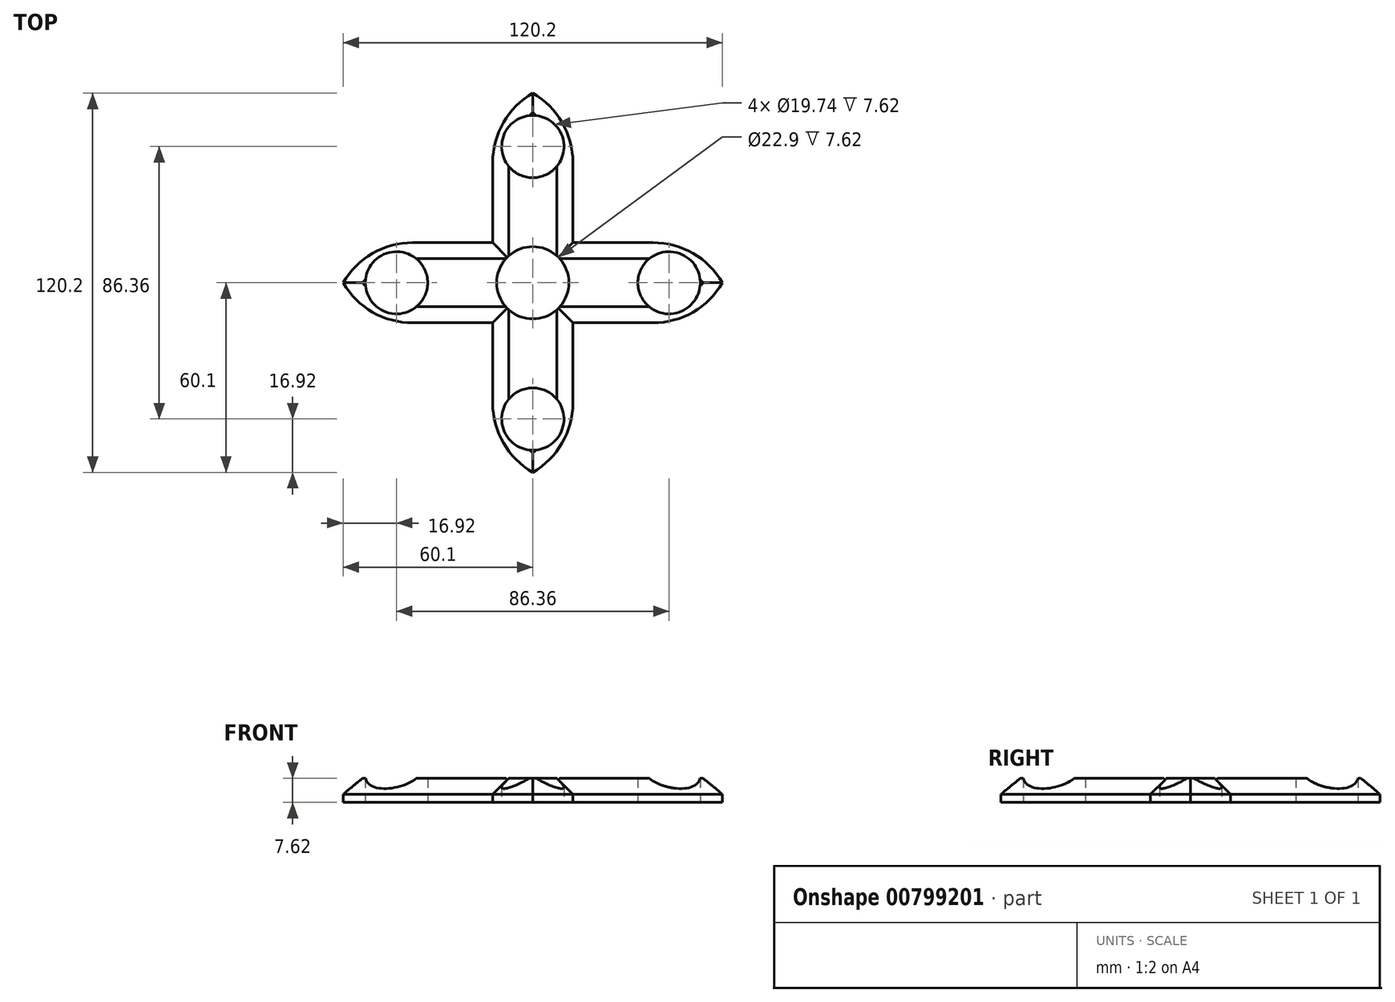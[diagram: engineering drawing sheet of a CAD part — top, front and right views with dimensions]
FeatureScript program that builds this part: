
annotation { "Feature Type Name" : "Feature", "Feature Type Description" : "" }
export const myFeature = defineFeature(function(context is Context, id is Id, definition is map)
    precondition{}
    {
        {
            var Q0;
            Q0=qCreatedBy(makeId("Top.planeOp"),FACE);
            var sketch = newSketch(context, id + "F0", { "sketchPlane" : qUnion([Q0])});
            skLineSegment(sketch, "E0.bottom", {"start": v(12.7, -38.1) * mm, "end": v(-12.7, -38.1) * mm});
            skLineSegment(sketch, "E0.top", {"start": v(12.7, 38.1) * mm, "end": v(-12.7, 38.1) * mm});
            skLineSegment(sketch, "E0.left", {"start": v(12.7, -38.1) * mm, "end": v(12.7, 38.1) * mm});
            skLineSegment(sketch, "E0.right", {"start": v(-12.7, -38.1) * mm, "end": v(-12.7, 38.1) * mm});
            skPoint(sketch, "E0.middle", {"position": v(0, 0) * mm});
            skLineSegment(sketch, "E1.bottom", {"start": v(38.1, -12.7) * mm, "end": v(-38.1, -12.7) * mm});
            skLineSegment(sketch, "E1.top", {"start": v(38.1, 12.7) * mm, "end": v(-38.1, 12.7) * mm});
            skLineSegment(sketch, "E1.left", {"start": v(38.1, -12.7) * mm, "end": v(38.1, 12.7) * mm});
            skLineSegment(sketch, "E1.right", {"start": v(-38.1, -12.7) * mm, "end": v(-38.1, 12.7) * mm});
            skCircle(sketch, "E2", {"center": v(0, 43.18) * mm, "radius": 9.87 * mm});
            skCircle(sketch, "E3", {"center": v(0, -43.18) * mm, "radius": 9.87 * mm});
            skPoint(sketch, "E3.centerSnap0", {"position": v(0, -12.7) * mm});
            skCircle(sketch, "E4", {"center": v(-43.18, 0) * mm, "radius": 9.87 * mm});
            skCircle(sketch, "E5", {"center": v(43.18, 0) * mm, "radius": 9.87 * mm});
            skPoint(sketch, "E5.centerSnap0", {"position": v(12.7, 0) * mm});
            skArc(sketch, "E6", {"start": v(-60.1, 0) * mm, "mid": v(-50.8, -9.3) * mm, "end": v(-38.1, -12.7) * mm});
            skArc(sketch, "E7", {"start": v(-38.1, 12.7) * mm, "mid": v(-50.8, 9.3) * mm, "end": v(-60.1, 0) * mm});
            skArc(sketch, "E8", {"start": v(0, 60.1) * mm, "mid": v(-9.3, 50.8) * mm, "end": v(-12.7, 38.1) * mm});
            skArc(sketch, "E9", {"start": v(12.7, 38.1) * mm, "mid": v(9.3, 50.8) * mm, "end": v(0, 60.1) * mm});
            skArc(sketch, "E10", {"start": v(60.1, 0) * mm, "mid": v(50.8, 9.3) * mm, "end": v(38.1, 12.7) * mm});
            skArc(sketch, "E11", {"start": v(38.1, -12.7) * mm, "mid": v(50.8, -9.3) * mm, "end": v(60.1, 0) * mm});
            skArc(sketch, "E12", {"start": v(-12.7, -38.1) * mm, "mid": v(-9.3, -50.8) * mm, "end": v(0, -60.1) * mm});
            skArc(sketch, "E13", {"start": v(0, -60.1) * mm, "mid": v(9.3, -50.8) * mm, "end": v(12.7, -38.1) * mm});
            skCircle(sketch, "E14", {"center": v(0, 0) * mm, "radius": 11.45 * mm});
            skSolve(sketch);
        }
        {
            var Q0;
            Q0=makeQuery(id+"F0.imprint","IMPRINT",FACE,{"disambiguationData":[TD([[makeQuery(id+"F0.imprint","IMPRINT",EDGE,{"derivedFrom":sQuery(id+"F0.wireOp",EDGE,"E14")}),-1.0]])]});
            var Q1;
            {var subQ5=sQuery(id+"F0.wireOp",EDGE,"E0.bottom");Q1=makeQuery(id+"F0.imprint","IMPRINT",FACE,{"disambiguationData":[TD([[makeQuery(id+"F0.imprint","IMPRINT",EDGE,{"derivedFrom":subQ5}),-1.0]])]});}
            var Q2;
            Q2=makeQuery(id+"F0.imprint","IMPRINT",FACE,{"disambiguationData":[TD([[makeQuery(id+"F0.imprint","IMPRINT",EDGE,{"derivedFrom":sQuery(id+"F0.wireOp",EDGE,"E0.bottom")}),1.0]])]});
            var Q3;
            Q3=makeQuery(id+"F0.imprint","IMPRINT",FACE,{"disambiguationData":[TD([[makeQuery(id+"F0.imprint","IMPRINT",EDGE,{"derivedFrom":sQuery(id+"F0.wireOp",EDGE,"E1.left")}),-1.0]])]});
            var Q4;
            {var subQ0=sQuery(id+"F0.wireOp",EDGE,"E1.left");Q4=makeQuery(id+"F0.imprint","IMPRINT",FACE,{"disambiguationData":[TD([[makeQuery(id+"F0.imprint","IMPRINT",EDGE,{"derivedFrom":subQ0}),1.0]])]});}
            var Q5;
            {var subQ5=sQuery(id+"F0.wireOp",EDGE,"E0.top");Q5=makeQuery(id+"F0.imprint","IMPRINT",FACE,{"disambiguationData":[TD([[makeQuery(id+"F0.imprint","IMPRINT",EDGE,{"derivedFrom":subQ5}),1.0]])]});}
            var Q6;
            Q6=makeQuery(id+"F0.imprint","IMPRINT",FACE,{"disambiguationData":[TD([[makeQuery(id+"F0.imprint","IMPRINT",EDGE,{"derivedFrom":sQuery(id+"F0.wireOp",EDGE,"E0.top")}),-1.0]])]});
            var Q7;
            Q7=makeQuery(id+"F0.imprint","IMPRINT",FACE,{"disambiguationData":[TD([[makeQuery(id+"F0.imprint","IMPRINT",EDGE,{"derivedFrom":sQuery(id+"F0.wireOp",EDGE,"E1.right")}),1.0]])]});
            var Q8;
            {var subQ0=sQuery(id+"F0.wireOp",EDGE,"E1.right");Q8=makeQuery(id+"F0.imprint","IMPRINT",FACE,{"disambiguationData":[TD([[makeQuery(id+"F0.imprint","IMPRINT",EDGE,{"derivedFrom":subQ0}),-1.0]])]});}
            extrude(context, id + "F1", {"entities" : qUnion([Q0, Q1, Q2, Q3, Q4, Q5, Q6, Q7, Q8]), "depth" : 7.62 * mm, "offsetDistance" : 25.4 * mm});
        }
        {
            var Q0;
            {var subQ0=sQuery(id+"F0.wireOp",EDGE,"E1.bottom");Q0=makeQuery(id+"F1.opExtrude","CAP_EDGE",EDGE,{"disambiguationData":[OSD([subQ0]),TDD([makeQuery(id+"F0.imprint","IMPRINT",EDGE,{"disambiguationData":[TD([[makeQuery(id+"F0.imprint","INTERSECT",VERTEX,{"derivedFrom":[sQuery(id+"F0.wireOp",EDGE,"E0.right"),subQ0]}),-1.0]])],"derivedFrom":subQ0})])],"isStart":false});}
            var Q1;
            {var subQ0=sQuery(id+"F0.wireOp",EDGE,"E0.right");Q1=makeQuery(id+"F1.opExtrude","CAP_EDGE",EDGE,{"disambiguationData":[OSD([subQ0]),TDD([makeQuery(id+"F0.imprint","IMPRINT",EDGE,{"disambiguationData":[TD([[makeQuery(id+"F0.imprint","INTERSECT",VERTEX,{"derivedFrom":[subQ0,sQuery(id+"F0.wireOp",EDGE,"E1.bottom")]}),1.0]])],"derivedFrom":subQ0})])],"isStart":false});}
            var Q2;
            {var subQ0=sQuery(id+"F0.wireOp",EDGE,"E0.left");Q2=makeQuery(id+"F1.opExtrude","CAP_EDGE",EDGE,{"disambiguationData":[OSD([subQ0]),TDD([makeQuery(id+"F0.imprint","IMPRINT",EDGE,{"disambiguationData":[TD([[makeQuery(id+"F0.imprint","INTERSECT",VERTEX,{"derivedFrom":[subQ0,sQuery(id+"F0.wireOp",EDGE,"E1.bottom")]}),1.0]])],"derivedFrom":subQ0})])],"isStart":false});}
            var Q3;
            {var subQ0=sQuery(id+"F0.wireOp",EDGE,"E1.bottom");Q3=makeQuery(id+"F1.opExtrude","CAP_EDGE",EDGE,{"disambiguationData":[OSD([subQ0]),TDD([makeQuery(id+"F0.imprint","IMPRINT",EDGE,{"disambiguationData":[TD([[makeQuery(id+"F0.imprint","INTERSECT",VERTEX,{"derivedFrom":[sQuery(id+"F0.wireOp",EDGE,"E0.left"),subQ0]}),1.0]])],"derivedFrom":subQ0})])],"isStart":false});}
            var Q4;
            {var subQ0=sQuery(id+"F0.wireOp",EDGE,"E1.top");Q4=makeQuery(id+"F1.opExtrude","CAP_EDGE",EDGE,{"disambiguationData":[OSD([subQ0]),TDD([makeQuery(id+"F0.imprint","IMPRINT",EDGE,{"disambiguationData":[TD([[makeQuery(id+"F0.imprint","INTERSECT",VERTEX,{"derivedFrom":[sQuery(id+"F0.wireOp",EDGE,"E0.left"),subQ0]}),1.0]])],"derivedFrom":subQ0})])],"isStart":false});}
            var Q5;
            {var subQ0=sQuery(id+"F0.wireOp",EDGE,"E0.left");Q5=makeQuery(id+"F1.opExtrude","CAP_EDGE",EDGE,{"disambiguationData":[OSD([subQ0]),TDD([makeQuery(id+"F0.imprint","IMPRINT",EDGE,{"disambiguationData":[TD([[makeQuery(id+"F0.imprint","INTERSECT",VERTEX,{"derivedFrom":[subQ0,sQuery(id+"F0.wireOp",EDGE,"E1.top")]}),-1.0]])],"derivedFrom":subQ0})])],"isStart":false});}
            var Q6;
            {var subQ0=sQuery(id+"F0.wireOp",EDGE,"E0.right");Q6=makeQuery(id+"F1.opExtrude","CAP_EDGE",EDGE,{"disambiguationData":[OSD([subQ0]),TDD([makeQuery(id+"F0.imprint","IMPRINT",EDGE,{"disambiguationData":[TD([[makeQuery(id+"F0.imprint","INTERSECT",VERTEX,{"derivedFrom":[subQ0,sQuery(id+"F0.wireOp",EDGE,"E1.top")]}),-1.0]])],"derivedFrom":subQ0})])],"isStart":false});}
            var Q7;
            {var subQ0=sQuery(id+"F0.wireOp",EDGE,"E1.top");Q7=makeQuery(id+"F1.opExtrude","CAP_EDGE",EDGE,{"disambiguationData":[OSD([subQ0]),TDD([makeQuery(id+"F0.imprint","IMPRINT",EDGE,{"disambiguationData":[TD([[makeQuery(id+"F0.imprint","INTERSECT",VERTEX,{"derivedFrom":[sQuery(id+"F0.wireOp",EDGE,"E0.right"),subQ0]}),-1.0]])],"derivedFrom":subQ0})])],"isStart":false});}
            chamfer(context, id + "F2", {"entities" : qUnion([Q0, Q1, Q2, Q3, Q4, Q5, Q6, Q7]), "width" : 5.08 * mm, "tangentPropagation" : true});
        }
    });
